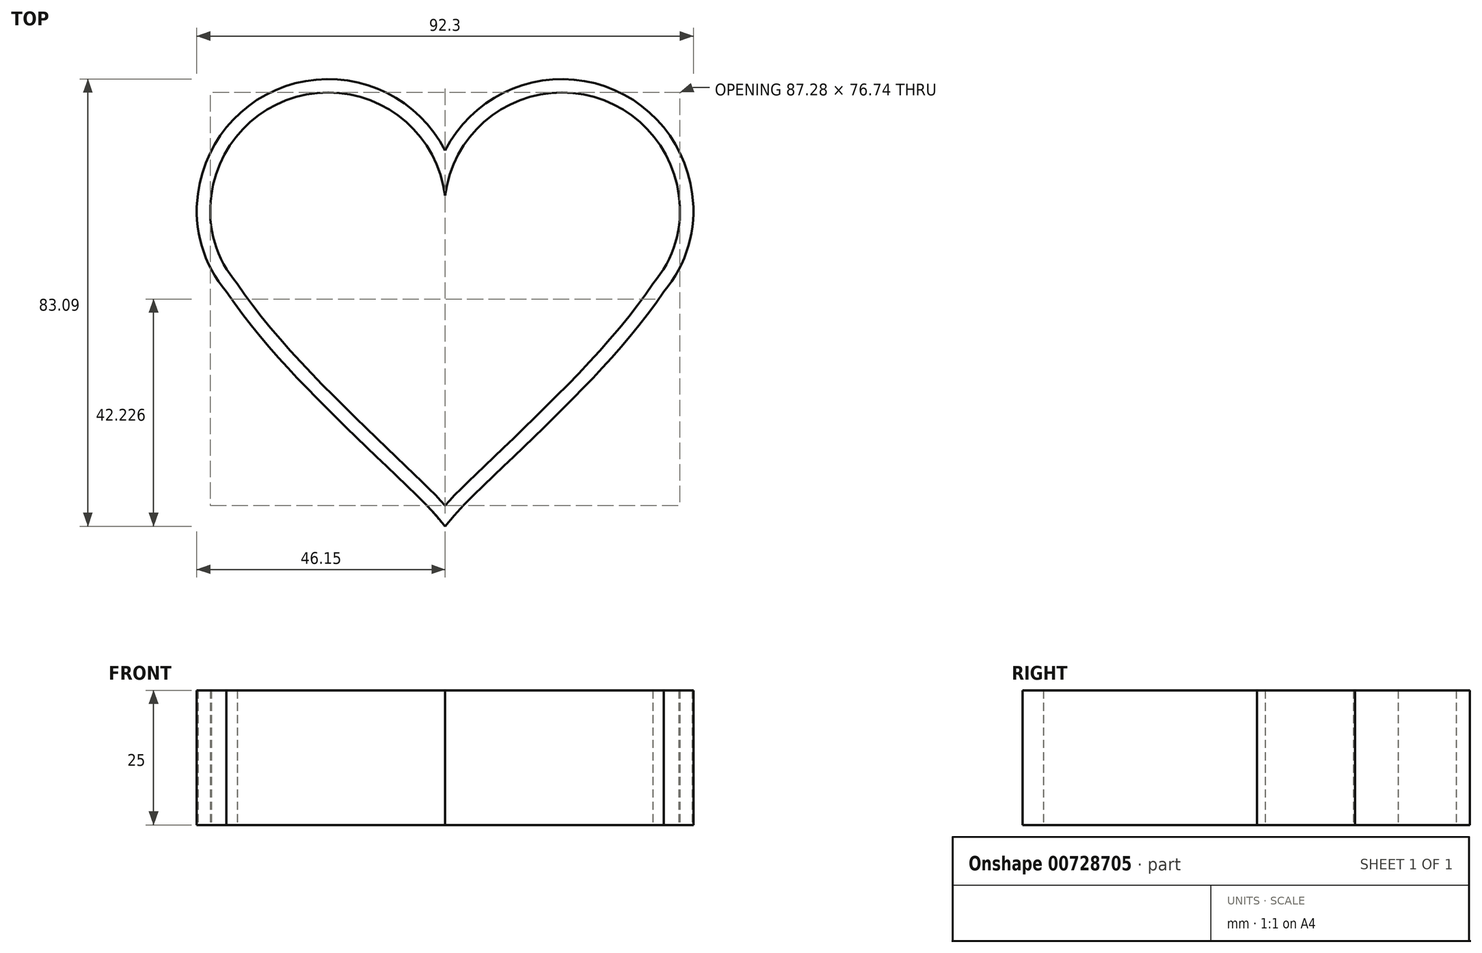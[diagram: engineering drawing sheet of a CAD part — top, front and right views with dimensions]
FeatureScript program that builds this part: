
annotation { "Feature Type Name" : "Feature", "Feature Type Description" : "" }
export const myFeature = defineFeature(function(context is Context, id is Id, definition is map)
    precondition{}
    {
        {
            var Q0;
            Q0=qCreatedBy(makeId("Top.planeOp"),FACE);
            var sketch = newSketch(context, id + "F0", { "sketchPlane" : qUnion([Q0])});
            skArc(sketch, "E0", {"start": v(43.45, 0) * mm, "mid": v(21.73, 19.13) * mm, "end": v(0, 0) * mm});
            skArc(sketch, "E1", {"start": v(38.6, -16.39) * mm, "mid": v(42.8, -8.72) * mm, "end": v(43.45, 0) * mm});
            skFitSpline(sketch, "E2", {"points": [v(38.6, -16.39) * mm, v(0, -57.6) * mm], "startDerivative": vector(-29.22, -45.3) * mm, "endDerivative": vector(-16.2, -19.03) * mm});
            skArc(sketch, "E3.MirrorCS", {"start": v(-43.45, 0) * mm, "mid": v(-21.73, 19.13) * mm, "end": v(0, 0) * mm});
            skArc(sketch, "E4.MirrorCS", {"start": v(-38.6, -16.39) * mm, "mid": v(-42.8, -8.72) * mm, "end": v(-43.45, 0) * mm});
            skFitSpline(sketch, "E5.MirrorCS", {"points": [v(-38.6, -16.39) * mm, v(0, -57.6) * mm], "startDerivative": vector(29.22, -45.3) * mm, "endDerivative": vector(16.2, -19.03) * mm});
            skSolve(sketch);
        }
        {
            var Q0;
            Q0=makeQuery(id+"F0.imprint","IMPRINT",FACE,{"disambiguationData":[TD([[makeQuery(id+"F0.imprint","IMPRINT",EDGE,{"derivedFrom":sQuery(id+"F0.wireOp",EDGE,"E0")}),1.0]])]});
            var Q1;
            Q1=sQuery(id+"F0.wireOp",EDGE,"E0");
            var Q2;
            Q2=sQuery(id+"F0.wireOp",EDGE,"E1");
            var Q3;
            Q3=sQuery(id+"F0.wireOp",EDGE,"E2");
            var Q4;
            Q4=sQuery(id+"F0.wireOp",EDGE,"E3.MirrorCS");
            var Q5;
            Q5=sQuery(id+"F0.wireOp",EDGE,"E5.MirrorCS");
            var Q6;
            Q6=sQuery(id+"F0.wireOp",EDGE,"E4.MirrorCS");
            extrude(context, id + "F1", {"entities" : qUnion([Q0]), "surfaceEntities" : qUnion([Q1, Q2, Q3, Q4, Q5, Q6]), "depth" : 25 * mm, "offsetDistance" : 25 * mm});
        }
        {
            var Q0;
            Q0=makeQuery(id+"F1.opExtrude","CAP_FACE",FACE,{"disambiguationData":[OSD([sQuery(id+"F0.wireOp",EDGE,"E0"),sQuery(id+"F0.wireOp",EDGE,"E1"),sQuery(id+"F0.wireOp",EDGE,"E2"),sQuery(id+"F0.wireOp",EDGE,"E3.MirrorCS"),sQuery(id+"F0.wireOp",EDGE,"E4.MirrorCS"),sQuery(id+"F0.wireOp",EDGE,"E5.MirrorCS")])],"isStart":false});
            var Q1;
            Q1=makeQuery(id+"F1.opExtrude","CAP_FACE",FACE,{"disambiguationData":[OSD([sQuery(id+"F0.wireOp",EDGE,"E0"),sQuery(id+"F0.wireOp",EDGE,"E1"),sQuery(id+"F0.wireOp",EDGE,"E2"),sQuery(id+"F0.wireOp",EDGE,"E3.MirrorCS"),sQuery(id+"F0.wireOp",EDGE,"E4.MirrorCS"),sQuery(id+"F0.wireOp",EDGE,"E5.MirrorCS")])],"isStart":true});
            var Q2;
            Q2=makeQuery(id+"F1.opExtrude","SWEPT_BODY",BODY,{"disambiguationData":[OSD([sQuery(id+"F0.wireOp",EDGE,"E0"),sQuery(id+"F0.wireOp",EDGE,"E1"),sQuery(id+"F0.wireOp",EDGE,"E2"),sQuery(id+"F0.wireOp",EDGE,"E3.MirrorCS"),sQuery(id+"F0.wireOp",EDGE,"E4.MirrorCS"),sQuery(id+"F0.wireOp",EDGE,"E5.MirrorCS")])]});
            shell(context, id + "F2", {"entities" : qUnion([Q0, Q1]), "parts" : qUnion([Q2]), "thickness" : 2.5 * mm, "oppositeDirection" : true});
        }
    });
